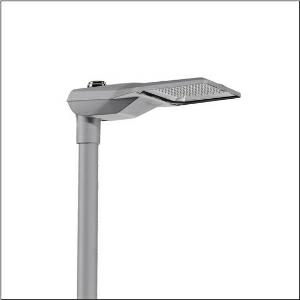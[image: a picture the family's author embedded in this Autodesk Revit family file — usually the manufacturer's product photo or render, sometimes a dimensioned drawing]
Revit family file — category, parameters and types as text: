
# Revit family: streetlight_sl_21_midi___st1_0a_5xe7d27n08mb_7be8
name_source: partatom
category: Lighting Fixtures
units: mm (PartAtom-declared; Revit-internal decimal feet)

## family parameters
Cut with Voids When Loaded = No
Host = Face
Light Source = No
Part Type = Normal
Room Calculation Point = No
Round Connector Dimension = Use Diameter
Shared = No

## types (1)
- --- (1 x LED, 14990 lm, 134.3 W, 2200K)
    Apparent Load = 134 VA
    CIE Flux Codes = 37 72 97 100 100
    Color Rendering = 70
    Color Temperature = 2200K
    Default Elevation = 1800 mm
    Description = Streetlight SL 21 midi, mast luminaire, primary light control with lens, of PMMA, primary optical cover: cover, of toughened safety glass, transparent, light distribution: ST1.0a, light emission: direct distribution, primary light characteristic: asymmetric, installation type: side-entry, LED, 3G 2.5mm², High Power LED, rated luminous flux: 14.990lm, luminous efficacy: 112lm/W, light colour: 722, colour temperature: 2200K, control gear: NEMA (7pin), control: overheat protection, pre-setting: linear dimming characteristic, constant luminous flux control, time-dependent luminous flux control, flexible luminous flux parameterisation, mains connection: 220..240V, AC, 50/60Hz, connection cable pre-assembled, cable length: 12,5m, wiring characteristics: H05VV-F, start of lifetime: 134W, end of service life: 141W, reduction: 60W, luminaire housing, of diecast aluminium (EN AC-44300), powder-coated, Siteco® metallic grey (DB 702S), corrosivity category C5 mid according to DIN EN ISO 12944, multi-level sealing system, sealing non-destructively replaceable, inclination adjustable: 0°, 5°, 10°, 15°, length: 644mm, width: 335mm, height: 110mm, spigot size: 42mm (side-entry), mounting height: 4..8m, protection rating (complete): IP66, insulation class (complete): insulation class I (protective earthing), certification: CE, ENEC, ENEC+, VDE, impact resistance: IK10, permissible operating ambient temperature for outdoor applications: -40..+50°C, standard-compliant lighting for roads and squares, packaging unit: 1 piece

Light Distribution: ST1.0a
    Height = 111 mm
    Lamp = 1 x LED
    Lamp Light Flux = 14990 lm
    Lamp Power = 134.3 W
    Lamp count = 1
    Length = 644 mm
    Luminous efficacy = 112 lm/W
    Manufacturer = Siteco
    ModVariant = No
    Model = 5XE7D27N08MB
    Number of Poles = 1
    OnlyDefault = Yes
    Power Factor = 1
    Product Name = Streetlight SL 21 midi | ST1.0a
    Product group = mast luminaire | pylon top
    ProductGroupID = 6100
    Protection Class = Protection class I
    Protection Degree = IP 66
    RLX_Detail_Level = 1
    RLX_Emergency_Light_Flux = 0 lm
    RLX_Emergency_Type = 0
    RLX_Emergency_Type_DB = No
    RlxData = <blob elided: 26481 chars, md5=36183441>
    Socket = socket
    Standby Power = 0 W
    System Light Flux = 14991 lm
    System Power = 134 W
    Type Comments = factory setting: luminous flux: 100 % | dim-lin: 254 | 687 mA
    Type Image = l_1294377.jpg
    URL = http://relux.com
    VarID = @adj_157605
    Voltage = 0 V
    Weight = 0.00 kg
    Width = 336 mm

## geometry (parser evidence)
native form markers: Blend x4, Sweep x12
no freeform markers — native parametric forms only
